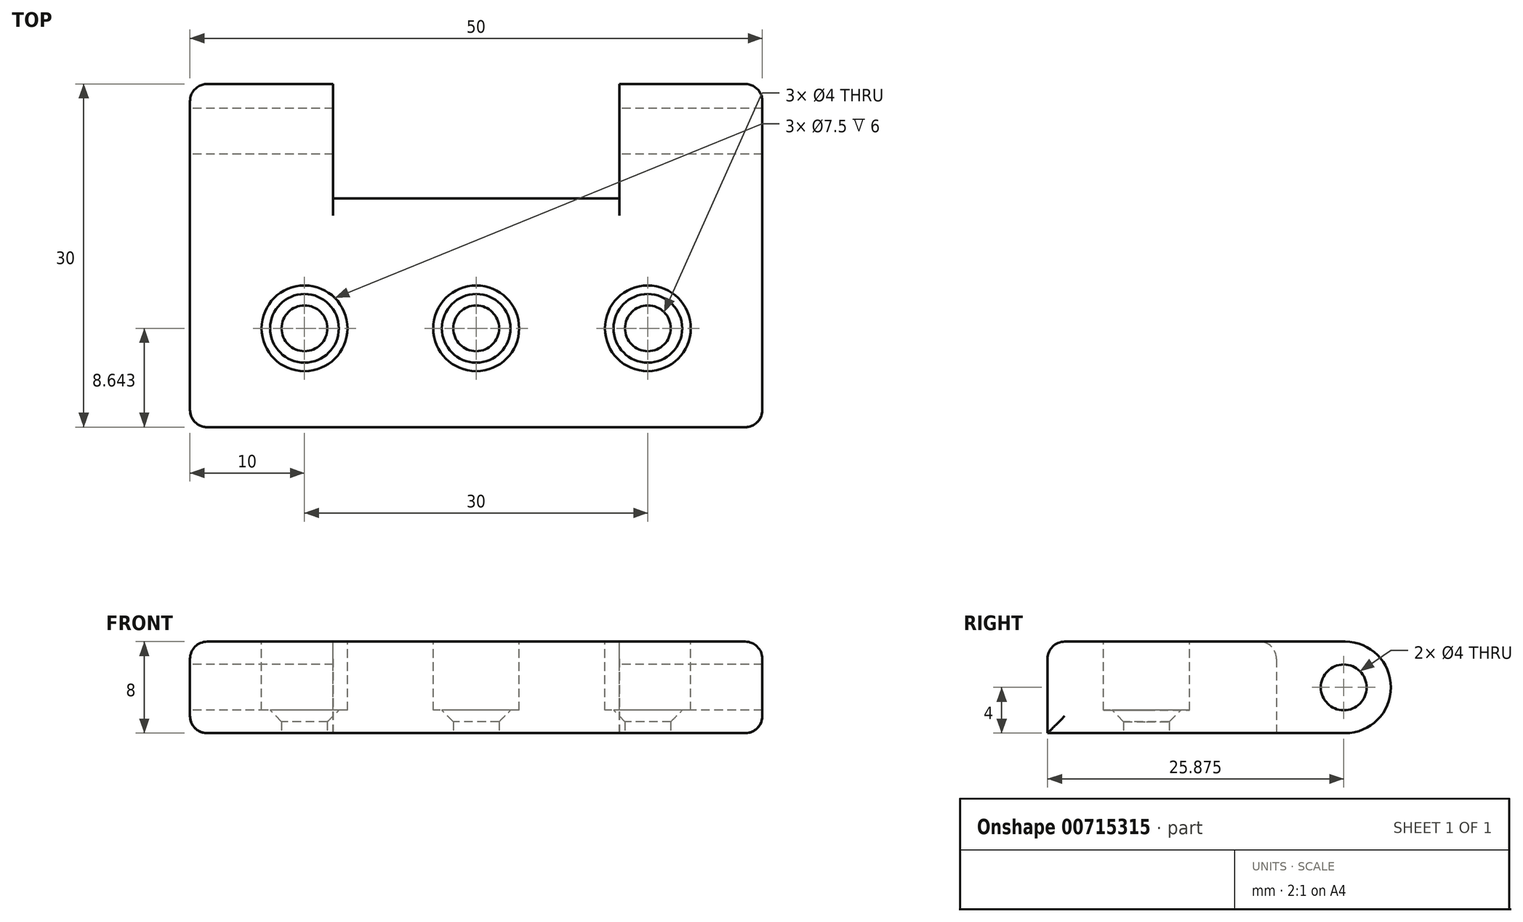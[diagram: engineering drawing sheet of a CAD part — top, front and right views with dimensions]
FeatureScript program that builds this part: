
annotation { "Feature Type Name" : "Feature", "Feature Type Description" : "" }
export const myFeature = defineFeature(function(context is Context, id is Id, definition is map)
    precondition{}
    {
        {
            var Q0;
            Q0=qCreatedBy(makeId("Top.planeOp"),FACE);
            var sketch = newSketch(context, id + "F0", { "sketchPlane" : qUnion([Q0])});
            skLineSegment(sketch, "E0.bottom", {"start": v(25, 15) * mm, "end": v(12.5, 15) * mm});
            skLineSegment(sketch, "E0.top", {"start": v(25, -15) * mm, "end": v(-25, -15) * mm});
            skLineSegment(sketch, "E0.left", {"start": v(25, 15) * mm, "end": v(25, -15) * mm});
            skLineSegment(sketch, "E0.right", {"start": v(-25, 15) * mm, "end": v(-25, -15) * mm});
            skPoint(sketch, "E0.middle", {"position": v(0, 0) * mm});
            skLineSegment(sketch, "E1.top", {"start": v(-12.5, 5) * mm, "end": v(12.5, 5) * mm});
            skLineSegment(sketch, "E1.left", {"start": v(-12.5, 15) * mm, "end": v(-12.5, 5) * mm});
            skLineSegment(sketch, "E1.right", {"start": v(12.5, 15) * mm, "end": v(12.5, 5) * mm});
            skLineSegment(sketch, "E2.trimOffspring", {"start": v(-12.5, 15) * mm, "end": v(-25, 15) * mm});
            skCircle(sketch, "E3", {"center": v(15, -6.36) * mm, "radius": 2 * mm});
            skCircle(sketch, "E4", {"center": v(-15, -6.36) * mm, "radius": 2 * mm});
            skCircle(sketch, "E5", {"center": v(0, -6.36) * mm, "radius": 2 * mm});
            skSolve(sketch);
        }
        {
            var Q0;
            Q0=makeQuery(id+"F0.imprint","IMPRINT",FACE,{"disambiguationData":[TD([[makeQuery(id+"F0.imprint","IMPRINT",EDGE,{"derivedFrom":sQuery(id+"F0.wireOp",EDGE,"E0.bottom")}),1.0]])]});
            extrude(context, id + "F1", {"entities" : qUnion([Q0]), "depth" : 8 * mm, "offsetDistance" : 25 * mm});
        }
        {
            var Q0;
            Q0=makeQuery(id+"F1.opExtrude","SWEPT_FACE",FACE,{"disambiguationData":[OSD([sQuery(id+"F0.wireOp",EDGE,"E0.right")])]});
            var sketch = newSketch(context, id + "F2", { "sketchPlane" : qUnion([Q0])});
            skCircle(sketch, "E6", {"center": v(-10.87, 4) * mm, "radius": 2 * mm});
            skPoint(sketch, "E6.centerSnap0", {"position": v(-15, 4) * mm});
            skSolve(sketch);
        }
        {
            var Q0;
            Q0 = qSketchRegion(id + "F2", true);
            extrude(context, id + "F3", {"entities" : qUnion([Q0]), "operationType" : NewBodyOperationType.REMOVE, "oppositeDirection" : true, "depth" : 60 * mm, "offsetDistance" : 25 * mm});
        }
        {
            var Q0;
            Q0=makeQuery(id+"F1.opExtrude","CAP_EDGE",EDGE,{"disambiguationData":[OSD([sQuery(id+"F0.wireOp",EDGE,"E2.trimOffspring")])],"isStart":false});
            var Q1;
            Q1=makeQuery(id+"F1.opExtrude","CAP_EDGE",EDGE,{"disambiguationData":[OSD([sQuery(id+"F0.wireOp",EDGE,"E0.bottom")])],"isStart":false});
            var Q2;
            Q2=makeQuery(id+"F1.opExtrude","CAP_EDGE",EDGE,{"disambiguationData":[OSD([sQuery(id+"F0.wireOp",EDGE,"E2.trimOffspring")])],"isStart":true});
            var Q3;
            Q3=makeQuery(id+"F1.opExtrude","CAP_EDGE",EDGE,{"disambiguationData":[OSD([sQuery(id+"F0.wireOp",EDGE,"E0.bottom")])],"isStart":true});
            fillet(context, id + "F4", {"entities" : qUnion([Q0, Q1, Q2, Q3]), "radius" : 4 * mm, "tangentPropagation" : true, "allowEdgeOverflow" : false});
        }
        {
            var Q0;
            Q0=makeQuery(id+"F1.opExtrude","CAP_EDGE",EDGE,{"disambiguationData":[OSD([sQuery(id+"F0.wireOp",EDGE,"E1.top")])],"isStart":false});
            var Q1;
            Q1=makeQuery(id+"F1.opExtrude","CAP_EDGE",EDGE,{"disambiguationData":[OSD([sQuery(id+"F0.wireOp",EDGE,"E0.top")])],"isStart":false});
            fillet(context, id + "F5", {"entities" : qUnion([Q0, Q1]), "radius" : 1.5 * mm, "tangentPropagation" : true, "allowEdgeOverflow" : false});
        }
        {
            var Q0;
            Q0=makeQuery(id+"F1.opExtrude","CAP_FACE",FACE,{"disambiguationData":[OSD([sQuery(id+"F0.wireOp",EDGE,"E0.bottom"),sQuery(id+"F0.wireOp",EDGE,"E0.top"),sQuery(id+"F0.wireOp",EDGE,"E0.left"),sQuery(id+"F0.wireOp",EDGE,"E0.right"),sQuery(id+"F0.wireOp",EDGE,"E1.top"),sQuery(id+"F0.wireOp",EDGE,"E1.left"),sQuery(id+"F0.wireOp",EDGE,"E1.right"),sQuery(id+"F0.wireOp",EDGE,"E2.trimOffspring"),sQuery(id+"F0.wireOp",EDGE,"E3"),sQuery(id+"F0.wireOp",EDGE,"E4"),sQuery(id+"F0.wireOp",EDGE,"E5")])],"isStart":false});
            var sketch = newSketch(context, id + "F6", { "sketchPlane" : qUnion([Q0])});
            skCircle(sketch, "E7", {"center": v(-15, -6.36) * mm, "radius": 3.75 * mm});
            skCircle(sketch, "E8", {"center": v(0, -6.36) * mm, "radius": 3.75 * mm});
            skCircle(sketch, "E9", {"center": v(15, -6.36) * mm, "radius": 3.75 * mm});
            skSolve(sketch);
        }
        {
            var Q0;
            Q0 = qSketchRegion(id + "F6", true);
            extrude(context, id + "F7", {"entities" : qUnion([Q0]), "operationType" : NewBodyOperationType.REMOVE, "oppositeDirection" : true, "depth" : 6 * mm, "offsetDistance" : 25 * mm});
        }
        {
            var Q0;
            Q0=makeQuery(id+"F7.boolean.opBoolean","INTERSECT",EDGE,{"derivedFrom":[makeQuery(id+"F1.opExtrude","SWEPT_FACE",FACE,{"disambiguationData":[OSD([sQuery(id+"F0.wireOp",EDGE,"E4")])]}),makeQuery(id+"F7.opExtrude","CAP_FACE",FACE,{"disambiguationData":[OSD([sQuery(id+"F6.wireOp",EDGE,"E7")])],"isStart":false})]});
            var Q1;
            Q1=makeQuery(id+"F7.boolean.opBoolean","INTERSECT",EDGE,{"derivedFrom":[makeQuery(id+"F1.opExtrude","SWEPT_FACE",FACE,{"disambiguationData":[OSD([sQuery(id+"F0.wireOp",EDGE,"E5")])]}),makeQuery(id+"F7.opExtrude","CAP_FACE",FACE,{"disambiguationData":[OSD([sQuery(id+"F6.wireOp",EDGE,"E8")])],"isStart":false})]});
            var Q2;
            Q2=makeQuery(id+"F7.boolean.opBoolean","INTERSECT",EDGE,{"derivedFrom":[makeQuery(id+"F1.opExtrude","SWEPT_FACE",FACE,{"disambiguationData":[OSD([sQuery(id+"F0.wireOp",EDGE,"E3")])]}),makeQuery(id+"F7.opExtrude","CAP_FACE",FACE,{"disambiguationData":[OSD([sQuery(id+"F6.wireOp",EDGE,"E9")])],"isStart":false})]});
            chamfer(context, id + "F8", {"entities" : qUnion([Q0, Q1, Q2]), "width" : 1 * mm, "tangentPropagation" : true});
        }
        {
            var Q0;
            Q0=makeQuery(id+"F1.opExtrude","CAP_EDGE",EDGE,{"disambiguationData":[OSD([sQuery(id+"F0.wireOp",EDGE,"E0.left")])],"isStart":false});
            var Q1;
            Q1=makeQuery(id+"F1.opExtrude","CAP_EDGE",EDGE,{"disambiguationData":[OSD([sQuery(id+"F0.wireOp",EDGE,"E0.right")])],"isStart":false});
            fillet(context, id + "F9", {"entities" : qUnion([Q0, Q1]), "radius" : 1.5 * mm, "tangentPropagation" : true, "allowEdgeOverflow" : false});
        }
    });
